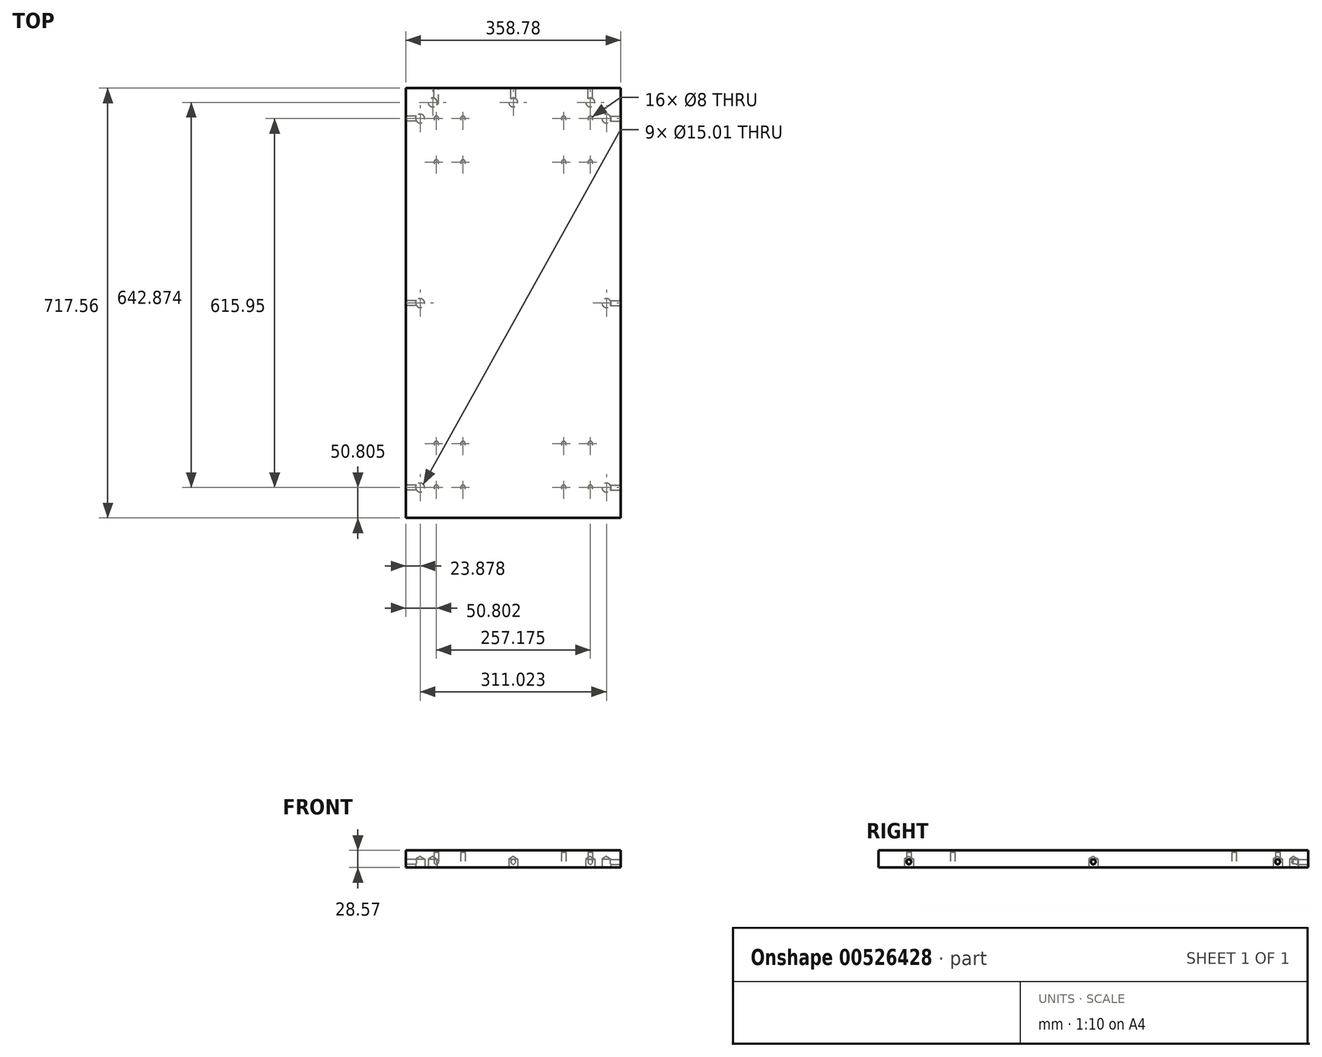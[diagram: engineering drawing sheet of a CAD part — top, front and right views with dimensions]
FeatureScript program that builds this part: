
annotation { "Feature Type Name" : "Feature", "Feature Type Description" : "" }
export const myFeature = defineFeature(function(context is Context, id is Id, definition is map)
    precondition{}
    {
        {
            var Q0;
            Q0=qCreatedBy(makeId("Top.planeOp"),FACE);
            var sketch = newSketch(context, id + "F0", { "sketchPlane" : qUnion([Q0])});
            skLineSegment(sketch, "E0.bottom", {"start": v(179.39, 358.78) * mm, "end": v(-179.39, 358.78) * mm});
            skLineSegment(sketch, "E0.top", {"start": v(179.39, -358.78) * mm, "end": v(-179.39, -358.78) * mm});
            skLineSegment(sketch, "E0.left", {"start": v(179.39, 358.77) * mm, "end": v(179.39, -358.78) * mm});
            skLineSegment(sketch, "E0.right", {"start": v(-179.39, 358.77) * mm, "end": v(-179.39, -358.78) * mm});
            skPoint(sketch, "E0.middle", {"position": v(0, 0) * mm});
            skSolve(sketch);
        }
        {
            var Q0;
            Q0=makeQuery(id+"F0.imprint","IMPRINT",FACE,{"disambiguationData":[TD([[makeQuery(id+"F0.imprint","IMPRINT",EDGE,{"derivedFrom":sQuery(id+"F0.wireOp",EDGE,"E0.bottom")}),1.0]])]});
            extrude(context, id + "F1", {"entities" : qUnion([Q0]), "depth" : 19.05 * mm, "offsetDistance" : 25.4 * mm});
        }
        {
            var Q0;
            Q0=makeQuery(id+"F1.opExtrude","SWEPT_FACE",FACE,{"disambiguationData":[OSD([sQuery(id+"F0.wireOp",EDGE,"E0.left")])]});
            var sketch = newSketch(context, id + "F2", { "sketchPlane" : qUnion([Q0])});
            skPoint(sketch, "E1", {"position": v(-307.98, 9.53) * mm});
            skPoint(sketch, "E2", {"position": v(0, 9.53) * mm});
            skPoint(sketch, "E3", {"position": v(307.97, 9.53) * mm});
            skSolve(sketch);
        }
        {
            var Q0;
            Q0=sQuery(id+"F2.wireOp",VERTEX,"E1");
            var Q1;
            Q1=sQuery(id+"F2.wireOp",VERTEX,"E2");
            var Q2;
            Q2=sQuery(id+"F2.wireOp",VERTEX,"E3");
            var Q3;
            Q3=makeQuery(id+"F1.opExtrude","SWEPT_BODY",BODY,{"disambiguationData":[OSD([sQuery(id+"F0.wireOp",EDGE,"E0.bottom"),sQuery(id+"F0.wireOp",EDGE,"E0.top"),sQuery(id+"F0.wireOp",EDGE,"E0.left"),sQuery(id+"F0.wireOp",EDGE,"E0.right")])]});
            hole(context, id + "F3", {"style" : HoleStyle.SIMPLE, "endStyle" : HoleEndStyle.BLIND, "holeDiameter" : 8 * mm, "holeDepth" : 25.4 * mm, "isTappedThrough" : true, "tappedDepth" : 12.7 * mm, "tapClearance" : 3, "startFromSketch" : true, "locations" : qUnion([Q0, Q1, Q2]), "scope" : qUnion([Q3])});
        }
        {
            var Q0;
            Q0=makeQuery(id+"F1.opExtrude","SWEPT_FACE",FACE,{"disambiguationData":[OSD([sQuery(id+"F0.wireOp",EDGE,"E0.right")])]});
            var sketch = newSketch(context, id + "F4", { "sketchPlane" : qUnion([Q0])});
            skPoint(sketch, "E4", {"position": v(0, 9.53) * mm});
            skPoint(sketch, "E5", {"position": v(307.98, 9.53) * mm});
            skPoint(sketch, "E6", {"position": v(-307.98, 9.53) * mm});
            skSolve(sketch);
        }
        {
            var Q0;
            Q0=sQuery(id+"F4.wireOp",VERTEX,"E6");
            var Q1;
            Q1=sQuery(id+"F4.wireOp",VERTEX,"E4");
            var Q2;
            Q2=sQuery(id+"F4.wireOp",VERTEX,"E5");
            var Q3;
            Q3=makeQuery(id+"F1.opExtrude","SWEPT_BODY",BODY,{"disambiguationData":[OSD([sQuery(id+"F0.wireOp",EDGE,"E0.bottom"),sQuery(id+"F0.wireOp",EDGE,"E0.top"),sQuery(id+"F0.wireOp",EDGE,"E0.left"),sQuery(id+"F0.wireOp",EDGE,"E0.right")])]});
            hole(context, id + "F5", {"style" : HoleStyle.SIMPLE, "endStyle" : HoleEndStyle.BLIND, "holeDiameter" : 8 * mm, "holeDepth" : 25.4 * mm, "isTappedThrough" : true, "tappedDepth" : 12.7 * mm, "tapClearance" : 3, "startFromSketch" : true, "locations" : qUnion([Q0, Q1, Q2]), "scope" : qUnion([Q3])});
        }
        {
            var Q0;
            Q0=makeQuery(id+"F1.opExtrude","SWEPT_FACE",FACE,{"disambiguationData":[OSD([sQuery(id+"F0.wireOp",EDGE,"E0.bottom")])]});
            var sketch = newSketch(context, id + "F6", { "sketchPlane" : qUnion([Q0])});
            skPoint(sketch, "E7", {"position": v(-128.59, 9.53) * mm});
            skPoint(sketch, "E8", {"position": v(0, 9.53) * mm});
            skPoint(sketch, "E9", {"position": v(128.59, 9.53) * mm});
            skSolve(sketch);
        }
        {
            var Q0;
            Q0=sQuery(id+"F6.wireOp",VERTEX,"E7");
            var Q1;
            Q1=sQuery(id+"F6.wireOp",VERTEX,"E8");
            var Q2;
            Q2=sQuery(id+"F6.wireOp",VERTEX,"E9");
            var Q3;
            Q3=makeQuery(id+"F1.opExtrude","SWEPT_BODY",BODY,{"disambiguationData":[OSD([sQuery(id+"F0.wireOp",EDGE,"E0.bottom"),sQuery(id+"F0.wireOp",EDGE,"E0.top"),sQuery(id+"F0.wireOp",EDGE,"E0.left"),sQuery(id+"F0.wireOp",EDGE,"E0.right")])]});
            hole(context, id + "F7", {"style" : HoleStyle.SIMPLE, "endStyle" : HoleEndStyle.BLIND, "holeDiameter" : 8 * mm, "holeDepth" : 25.4 * mm, "isTappedThrough" : true, "tappedDepth" : 12.7 * mm, "tapClearance" : 3, "startFromSketch" : true, "locations" : qUnion([Q0, Q1, Q2]), "scope" : qUnion([Q3])});
        }
        {
            var Q0;
            Q0=makeQuery(id+"F1.opExtrude","CAP_FACE",FACE,{"disambiguationData":[OSD([sQuery(id+"F0.wireOp",EDGE,"E0.bottom"),sQuery(id+"F0.wireOp",EDGE,"E0.top"),sQuery(id+"F0.wireOp",EDGE,"E0.left"),sQuery(id+"F0.wireOp",EDGE,"E0.right")])],"isStart":true});
            var sketch = newSketch(context, id + "F8", { "sketchPlane" : qUnion([Q0])});
            skLineSegment(sketch, "E10", {"start": v(-179.39, 358.78) * mm, "end": v(-155.51, 358.78) * mm});
            skPoint(sketch, "E11", {"position": v(-134.62, -334.9) * mm});
            skPoint(sketch, "E12", {"position": v(0, -334.9) * mm});
            skPoint(sketch, "E13", {"position": v(128.59, -334.9) * mm});
            skPoint(sketch, "E14", {"position": v(155.51, -307.98) * mm});
            skPoint(sketch, "E15", {"position": v(-155.51, -307.98) * mm});
            skPoint(sketch, "E16", {"position": v(-155.51, 307.97) * mm});
            skPoint(sketch, "E17", {"position": v(155.51, 307.97) * mm});
            skPoint(sketch, "E18", {"position": v(155.51, 0) * mm});
            skPoint(sketch, "E19", {"position": v(-155.51, 0) * mm});
            skSolve(sketch);
        }
        {
            var Q0;
            Q0=sQuery(id+"F8.wireOp",VERTEX,"E16");
            var Q1;
            Q1=sQuery(id+"F8.wireOp",VERTEX,"E17");
            var Q2;
            Q2=sQuery(id+"F8.wireOp",VERTEX,"E18");
            var Q3;
            Q3=sQuery(id+"F8.wireOp",VERTEX,"E19");
            var Q4;
            Q4=sQuery(id+"F8.wireOp",VERTEX,"E15");
            var Q5;
            Q5=sQuery(id+"F8.wireOp",VERTEX,"E11");
            var Q6;
            Q6=sQuery(id+"F8.wireOp",VERTEX,"E12");
            var Q7;
            Q7=sQuery(id+"F8.wireOp",VERTEX,"E13");
            var Q8;
            Q8=sQuery(id+"F8.wireOp",VERTEX,"E14");
            var Q9;
            Q9=makeQuery(id+"F1.opExtrude","SWEPT_BODY",BODY,{"disambiguationData":[OSD([sQuery(id+"F0.wireOp",EDGE,"E0.bottom"),sQuery(id+"F0.wireOp",EDGE,"E0.top"),sQuery(id+"F0.wireOp",EDGE,"E0.left"),sQuery(id+"F0.wireOp",EDGE,"E0.right")])]});
            hole(context, id + "F9", {"style" : HoleStyle.SIMPLE, "endStyle" : HoleEndStyle.BLIND, "holeDiameter" : 15 * mm, "holeDepth" : 14.22 * mm, "isTappedThrough" : true, "tappedDepth" : 12.7 * mm, "tapClearance" : 3, "startFromSketch" : true, "locations" : qUnion([Q0, Q1, Q2, Q3, Q4, Q5, Q6, Q7, Q8]), "scope" : qUnion([Q9])});
        }
        {
            var Q0;
            Q0=makeQuery(id+"F1.opExtrude","CAP_FACE",FACE,{"disambiguationData":[OSD([sQuery(id+"F0.wireOp",EDGE,"E0.bottom"),sQuery(id+"F0.wireOp",EDGE,"E0.top"),sQuery(id+"F0.wireOp",EDGE,"E0.left"),sQuery(id+"F0.wireOp",EDGE,"E0.right")])],"isStart":false});
            extrude(context, id + "F10", {"entities" : qUnion([Q0]), "operationType" : NewBodyOperationType.ADD, "depth" : 9.52 * mm, "offsetDistance" : 25.4 * mm});
        }
        {
            var Q0;
            Q0=makeQuery(id+"F1.opExtrude","CAP_FACE",FACE,{"disambiguationData":[OSD([sQuery(id+"F0.wireOp",EDGE,"E0.bottom"),sQuery(id+"F0.wireOp",EDGE,"E0.top"),sQuery(id+"F0.wireOp",EDGE,"E0.left"),sQuery(id+"F0.wireOp",EDGE,"E0.right")])],"isStart":true});
            var sketch = newSketch(context, id + "F11", { "sketchPlane" : qUnion([Q0])});
            skLineSegment(sketch, "E20", {"start": v(-179.39, 358.78) * mm, "end": v(-128.59, 358.78) * mm});
            skLineSegment(sketch, "E21", {"start": v(-128.59, 358.78) * mm, "end": v(-128.59, 307.98) * mm});
            skLineSegment(sketch, "E22", {"start": v(-128.59, 307.98) * mm, "end": v(-84.14, 307.98) * mm});
            skLineSegment(sketch, "E23", {"start": v(-84.14, 307.98) * mm, "end": v(-84.14, 234.95) * mm});
            skLineSegment(sketch, "E24", {"start": v(-84.14, 234.95) * mm, "end": v(-128.59, 234.95) * mm});
            skLineSegment(sketch, "E25", {"start": v(-128.59, 234.95) * mm, "end": v(-128.59, 307.98) * mm});
            skLineSegment(sketch, "E26", {"start": v(179.39, 358.78) * mm, "end": v(128.59, 358.78) * mm});
            skLineSegment(sketch, "E27", {"start": v(128.59, 358.78) * mm, "end": v(128.59, 307.98) * mm});
            skLineSegment(sketch, "E28", {"start": v(128.59, 307.98) * mm, "end": v(84.14, 307.98) * mm});
            skLineSegment(sketch, "E29", {"start": v(84.14, 307.98) * mm, "end": v(84.14, 234.95) * mm});
            skLineSegment(sketch, "E30", {"start": v(84.14, 234.95) * mm, "end": v(128.59, 234.95) * mm});
            skLineSegment(sketch, "E31", {"start": v(128.59, 234.95) * mm, "end": v(128.59, 307.98) * mm});
            skLineSegment(sketch, "E32", {"start": v(179.39, -358.78) * mm, "end": v(128.59, -358.78) * mm});
            skLineSegment(sketch, "E33", {"start": v(128.59, -358.77) * mm, "end": v(128.59, -307.98) * mm});
            skLineSegment(sketch, "E34", {"start": v(128.59, -307.98) * mm, "end": v(84.14, -307.98) * mm});
            skLineSegment(sketch, "E35", {"start": v(84.14, -307.98) * mm, "end": v(84.14, -234.95) * mm});
            skLineSegment(sketch, "E36", {"start": v(84.14, -234.95) * mm, "end": v(128.59, -234.95) * mm});
            skLineSegment(sketch, "E37", {"start": v(128.59, -234.95) * mm, "end": v(128.59, -307.98) * mm});
            skLineSegment(sketch, "E38", {"start": v(-179.39, -358.78) * mm, "end": v(-128.59, -358.78) * mm});
            skLineSegment(sketch, "E39", {"start": v(-128.59, -358.78) * mm, "end": v(-128.59, -307.98) * mm});
            skLineSegment(sketch, "E40", {"start": v(-128.59, -307.98) * mm, "end": v(-84.14, -307.98) * mm});
            skLineSegment(sketch, "E41", {"start": v(-84.14, -307.98) * mm, "end": v(-84.14, -234.95) * mm});
            skLineSegment(sketch, "E42", {"start": v(-84.14, -234.95) * mm, "end": v(-128.59, -234.95) * mm});
            skLineSegment(sketch, "E43", {"start": v(-128.59, -234.95) * mm, "end": v(-128.59, -307.98) * mm});
            skSolve(sketch);
        }
        {
            var Q0;
            Q0=sQuery(id+"F11.wireOp",VERTEX,"E25.end");
            var Q1;
            Q1=sQuery(id+"F11.wireOp",VERTEX,"E23.start");
            var Q2;
            Q2=sQuery(id+"F11.wireOp",VERTEX,"E23.end");
            var Q3;
            Q3=sQuery(id+"F11.wireOp",VERTEX,"E24.end");
            var Q4;
            Q4=sQuery(id+"F11.wireOp",VERTEX,"E29.start");
            var Q5;
            Q5=sQuery(id+"F11.wireOp",VERTEX,"E28.start");
            var Q6;
            Q6=sQuery(id+"F11.wireOp",VERTEX,"E31.start");
            var Q7;
            Q7=sQuery(id+"F11.wireOp",VERTEX,"E30.start");
            var Q8;
            Q8=sQuery(id+"F11.wireOp",VERTEX,"E37.start");
            var Q9;
            Q9=sQuery(id+"F11.wireOp",VERTEX,"E36.start");
            var Q10;
            Q10=sQuery(id+"F11.wireOp",VERTEX,"E34.end");
            var Q11;
            Q11=sQuery(id+"F11.wireOp",VERTEX,"E33.end");
            var Q12;
            Q12=sQuery(id+"F11.wireOp",VERTEX,"E41.end");
            var Q13;
            Q13=sQuery(id+"F11.wireOp",VERTEX,"E42.end");
            var Q14;
            Q14=sQuery(id+"F11.wireOp",VERTEX,"E43.end");
            var Q15;
            Q15=sQuery(id+"F11.wireOp",VERTEX,"E40.end");
            var Q16;
            Q16=makeQuery(id+"F1.opExtrude","SWEPT_BODY",BODY,{"disambiguationData":[OSD([sQuery(id+"F0.wireOp",EDGE,"E0.bottom"),sQuery(id+"F0.wireOp",EDGE,"E0.top"),sQuery(id+"F0.wireOp",EDGE,"E0.left"),sQuery(id+"F0.wireOp",EDGE,"E0.right")])]});
            hole(context, id + "F12", {"style" : HoleStyle.SIMPLE, "endStyle" : HoleEndStyle.BLIND, "holeDiameter" : 8 * mm, "holeDepth" : 25.4 * mm, "isTappedThrough" : true, "tappedDepth" : 12.7 * mm, "tapClearance" : 3, "startFromSketch" : true, "locations" : qUnion([Q0, Q1, Q2, Q3, Q4, Q5, Q6, Q7, Q8, Q9, Q10, Q11, Q12, Q13, Q14, Q15]), "scope" : qUnion([Q16])});
        }
    });
